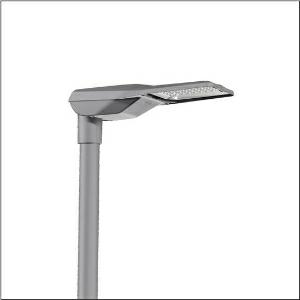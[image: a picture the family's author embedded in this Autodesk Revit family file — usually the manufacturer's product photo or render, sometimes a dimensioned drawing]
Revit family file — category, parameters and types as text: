
# Revit family: streetlight_sl_21_iq_mini___st0_5a_5xe2b31d08hb_2e1a
name_source: partatom
category: Lighting Fixtures
units: mm (PartAtom-declared; Revit-internal decimal feet)

## family parameters
Cut with Voids When Loaded = No
Host = Face
Light Source = No
Part Type = Normal
Room Calculation Point = No
Round Connector Dimension = Use Diameter
Shared = No

## types (1)
- --- (1 x LED, 9450 lm, 70.9 W, 3000K)
    Apparent Load = 71 VA
    CIE Flux Codes = 41 75 97 100 100
    Color Rendering = 70
    Color Temperature = 3000K
    Default Elevation = 1800 mm
    Description = Streetlight SL 21 iQ mini, mast luminaire, primary light control with lens, of PMMA, primary optical cover: cover, of toughened safety glass, transparent, light distribution: ST0.5a, light emission: direct distribution, primary light characteristic: asymmetric, installation type: post-top, side-entry, LED, High Power LED, rated luminous flux: 9.450lm, luminous efficacy: 133lm/W, light colour: 730, colour temperature: 3000K, control gear: iQ-Comfort, control: Auto-Match, Temp-Guard, Lumen-Switch, Night-Set, Smart-Wire, Light-Fading, Desk-Remote (wireless, voltage-free reading and setting of iQ features in the workshop via application-optimized NFC function/RFID function), optimised constant luminous flux control (CLO 2.0), pre-setting: linear dimming characteristic, mains connection: 220..240V, AC, 50/60Hz, start of lifetime: 71W, end of service life: 75W, reduction: 31W, luminaire housing, of diecast aluminium, powder-coated, Siteco® metallic grey (DB 702S), corrosivity category C5 mid according to DIN EN ISO 12944, please order mast flange separately, inclination adjustable: 0°, 5°, 10°, 15°, sealing non-destructively replaceable, multi-level sealing system, length: 628mm, width: 235mm, height: 110mm, mast flange for spigot size: 42mm (side-entry): 5XC10008XM4, 60/48mm (side-entry/post-top): 5XC10108XM2, 76/60mm (side-entry/post-top): 5XC10108XM1, mounting height: 4..8m, protection rating (complete): IP66, insulation class (complete): insulation class II (safety insulation), certification: CE, ENEC, ENEC+, VDE, impact resistance: IK10, permissible operating ambient temperature for outdoor applications: -40..+50°C, standard-compliant lighting for roads and squares, packaging unit: 1 piece

Light Distribution: ST0.5a
    Height = 110 mm
    Lamp = 1 x LED
    Lamp Light Flux = 9450 lm
    Lamp Power = 70.9 W
    Lamp count = 1
    Length = 625 mm
    Luminous efficacy = 133 lm/W
    Manufacturer = Siteco
    ModVariant = No
    Model = 5XE2B31D08HB
    Number of Poles = 1
    OnlyDefault = Yes
    Power Factor = 1
    Product Name = Streetlight SL 21 iQ mini | ST0.5a
    Product group = mast luminaire | pylon top
    ProductGroupID = 6100
    Protection Class = Protection class II
    Protection Degree = IP 66
    RLX_Detail_Level = 1
    RLX_Emergency_Light_Flux = 0 lm
    RLX_Emergency_Type = 0
    RLX_Emergency_Type_DB = No
    RlxData = <blob elided: 37333 chars, md5=66c20a68>
    Socket = socket
    Standby Power = 0 W
    System Light Flux = 9450 lm
    System Power = 71 W
    Type Comments = factory setting: luminous flux: 100 % | dim-lin: 254 | 711 mA
    Type Image = l_1003519.jpg
    URL = http://relux.com
    VarID = @adj_180085
    Voltage = 0 V
    Weight = 0.00 kg
    Width = 234 mm

## geometry (parser evidence)
native form markers: Blend x4, Sweep x12
no freeform markers — native parametric forms only
